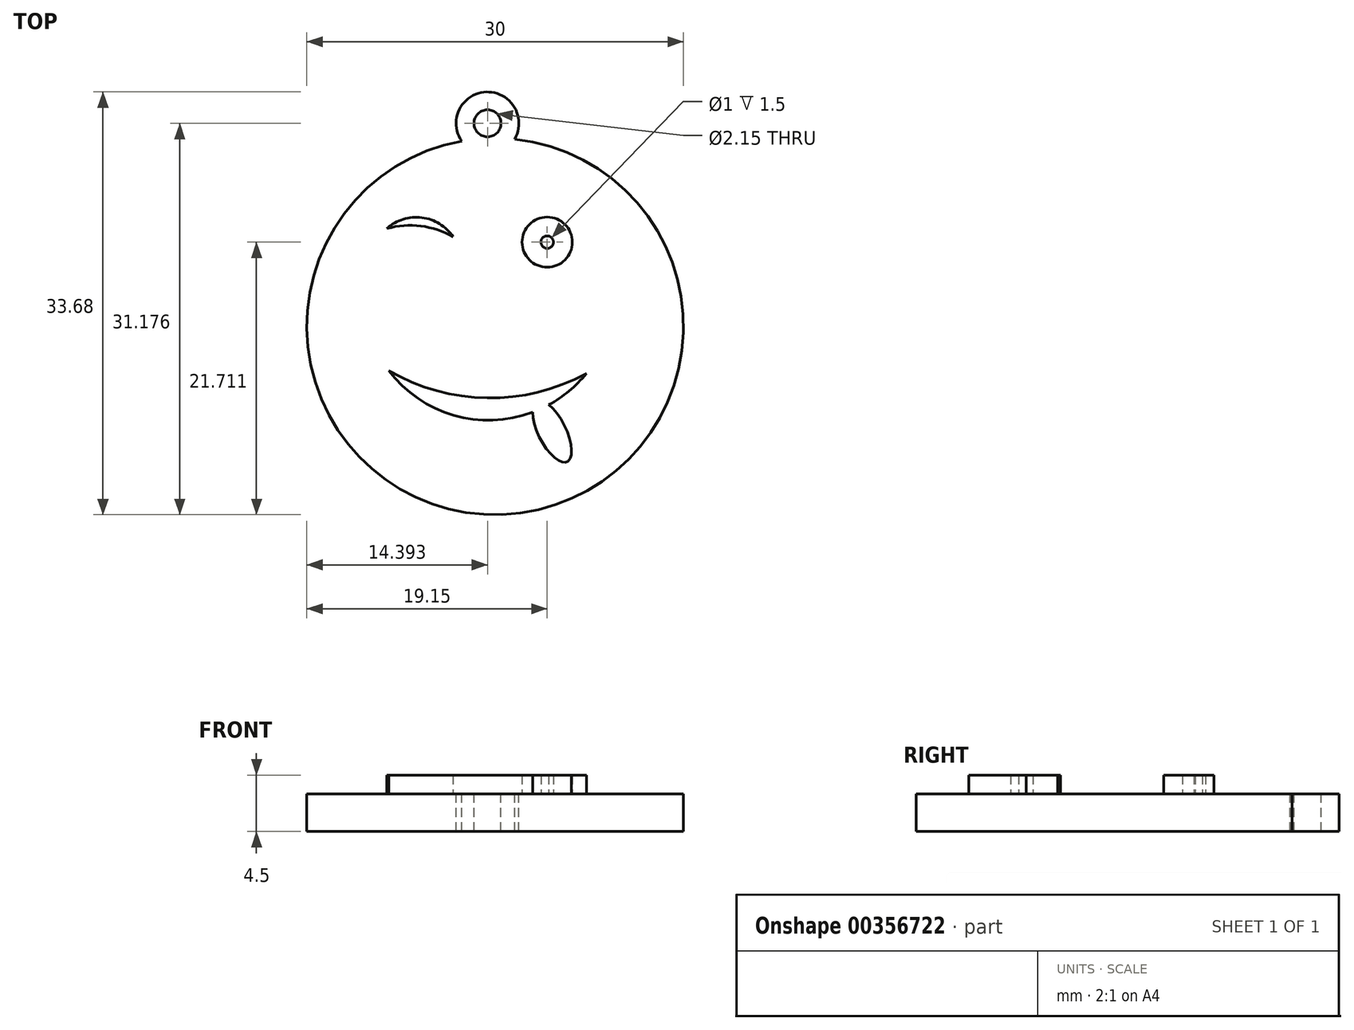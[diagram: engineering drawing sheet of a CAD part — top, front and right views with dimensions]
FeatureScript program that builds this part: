
annotation { "Feature Type Name" : "Feature", "Feature Type Description" : "" }
export const myFeature = defineFeature(function(context is Context, id is Id, definition is map)
    precondition{}
    {
        {
            var Q0;
            Q0=qCreatedBy(makeId("Top.planeOp"),FACE);
            var sketch = newSketch(context, id + "F0", { "sketchPlane" : qUnion([Q0])});
            skCircle(sketch, "E0", {"center": v(-16.15, 10.89) * mm, "radius": 15 * mm});
            skSolve(sketch);
        }
        {
            var Q0;
            Q0=makeQuery(id+"F0.imprint","IMPRINT",FACE,{"disambiguationData":[TD([[makeQuery(id+"F0.imprint","IMPRINT",EDGE,{"derivedFrom":sQuery(id+"F0.wireOp",EDGE,"E0")}),1.0]])]});
            extrude(context, id + "F1", {"entities" : qUnion([Q0]), "depth" : 3 * mm});
        }
        {
            var Q0;
            Q0=makeQuery(id+"F1.opExtrude","CAP_FACE",FACE,{"disambiguationData":[OSD([sQuery(id+"F0.wireOp",EDGE,"E0")])],"isStart":false});
            var sketch = newSketch(context, id + "F2", { "sketchPlane" : qUnion([Q0])});
            skCircle(sketch, "E1", {"center": v(-12, 17.6) * mm, "radius": 2 * mm});
            skArc(sketch, "E2", {"start": v(-24.63, 7.37) * mm, "mid": v(-19.45, 3.81) * mm, "end": v(-13.17, 4.05) * mm});
            skArc(sketch, "E3", {"start": v(-24.63, 7.37) * mm, "mid": v(-16.79, 5.18) * mm, "end": v(-8.88, 7.14) * mm});
            skArc(sketch, "E4.trimOffspring", {"start": v(-11.87, 4.64) * mm, "mid": v(-10.25, 5.74) * mm, "end": v(-8.88, 7.14) * mm});
            skEllipticalArc(sketch, "E5", {});
            skLineSegment(sketch, "E6", {"start": v(-12.3, 3.86) * mm, "end": v(-11.15, 1.48) * mm});
            skCircle(sketch, "E7", {"center": v(-12, 17.6) * mm, "radius": 0.5 * mm});
            skArc(sketch, "E8", {"start": v(-19.5, 18.02) * mm, "mid": v(-21.98, 19.56) * mm, "end": v(-24.77, 18.68) * mm});
            skArc(sketch, "E9", {"start": v(-19.5, 18.02) * mm, "mid": v(-22.07, 18.88) * mm, "end": v(-24.77, 18.68) * mm});
            const initialGuessF2  = {"E5": [-0.011616117766789846, 0.0025096476183439726, 0.44721347863836025, -0.8944272494307052, 0.002689783794368893, 0.0010980988702499518, 3.8341028207603642, 2.4206194368851324]};
            skSetInitialGuess(sketch, initialGuessF2);
            skSolve(sketch);
        }
        {
            var Q0;
            Q0 = qSketchRegion(id + "F2", true);
            extrude(context, id + "F3", {"entities" : qUnion([Q0]), "operationType" : NewBodyOperationType.ADD, "depth" : 1.5 * mm});
        }
        {
            var Q0;
            Q0=makeQuery(id+"F2.imprint","IMPRINT",FACE,{"disambiguationData":[TD([[makeQuery(id+"F2.imprint","IMPRINT",EDGE,{"derivedFrom":sQuery(id+"F2.wireOp",EDGE,"E1")}),-1.0]])]});
            var sketch = newSketch(context, id + "F4", { "sketchPlane" : qUnion([Q0])});
            skCircle(sketch, "E10", {"center": v(-16.76, 27.07) * mm, "radius": 2.5 * mm});
            skCircle(sketch, "E11", {"center": v(-16.76, 27.07) * mm, "radius": 1.07 * mm});
            skSolve(sketch);
        }
        {
            var Q0;
            Q0 = qSketchRegion(id + "F4", true);
            extrude(context, id + "F5", {"entities" : qUnion([Q0]), "operationType" : NewBodyOperationType.ADD, "oppositeDirection" : true, "depth" : 3 * mm});
        }
    });
